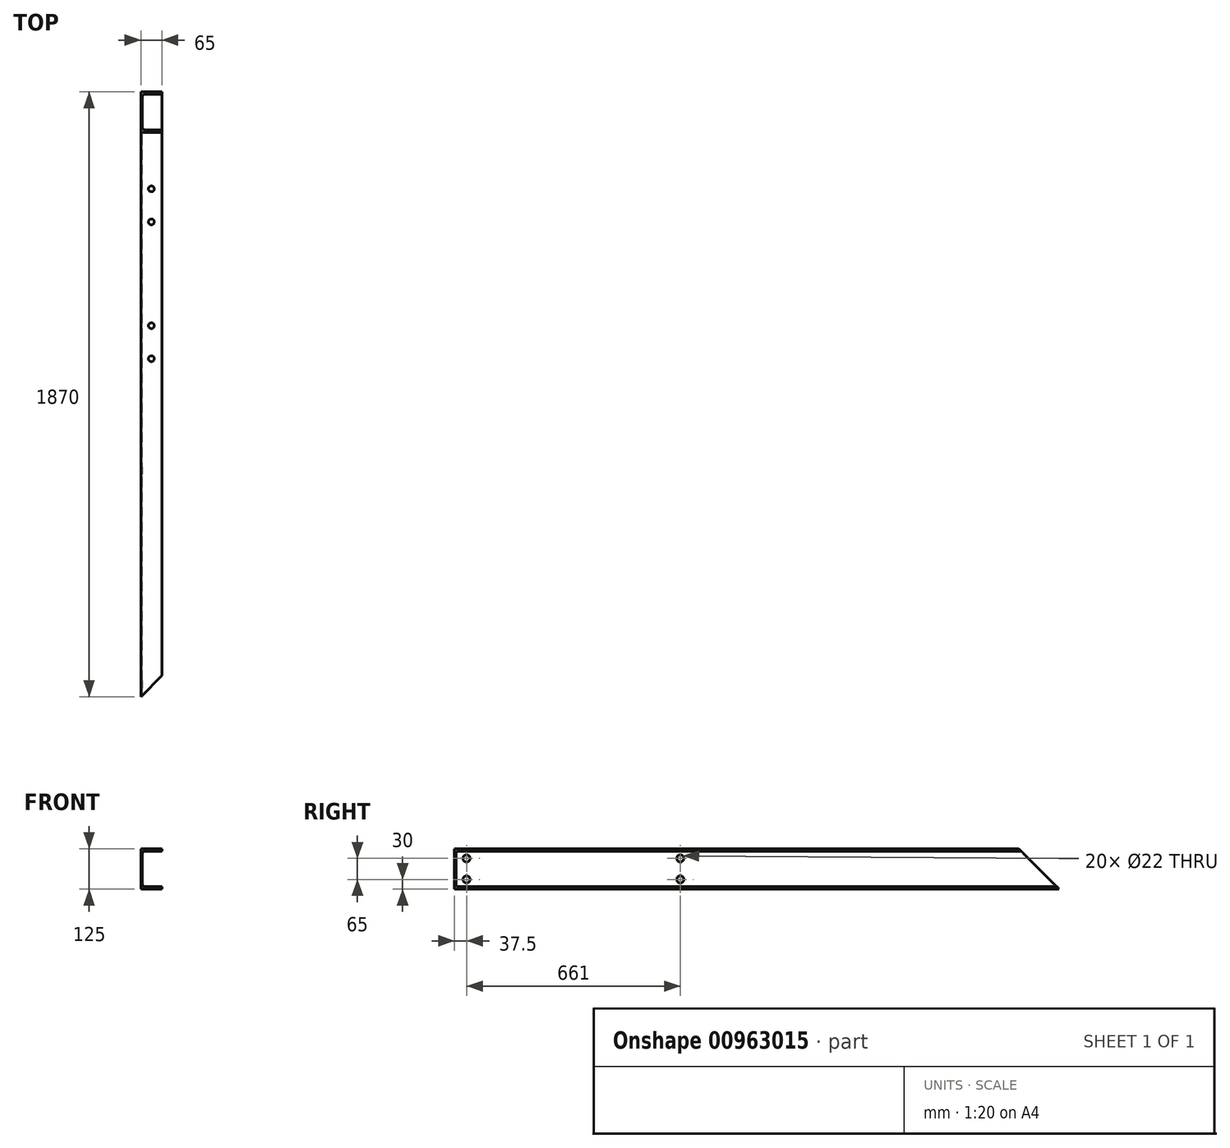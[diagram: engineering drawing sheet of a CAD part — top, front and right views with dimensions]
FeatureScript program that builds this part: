
annotation { "Feature Type Name" : "Feature", "Feature Type Description" : "" }
export const myFeature = defineFeature(function(context is Context, id is Id, definition is map)
    precondition{}
    {
        {
            var Q0;
            Q0=qCreatedBy(makeId("Front.planeOp"),FACE);
            var sketch = newSketch(context, id + "F0", { "sketchPlane" : qUnion([Q0])});
            skLineSegment(sketch, "E0", {"start": v(-25.17, -62.5) * mm, "end": v(-25.17, 62.5) * mm});
            skLineSegment(sketch, "E1", {"start": v(-25.17, 62.5) * mm, "end": v(39.83, 62.5) * mm});
            skLineSegment(sketch, "E2", {"start": v(39.83, 62.5) * mm, "end": v(39.83, 55) * mm});
            skLineSegment(sketch, "E3", {"start": v(39.83, 55) * mm, "end": v(-12.47, 55) * mm});
            skLineSegment(sketch, "E4", {"start": v(-25.17, -62.5) * mm, "end": v(39.83, -62.5) * mm});
            skLineSegment(sketch, "E5", {"start": v(39.83, -62.5) * mm, "end": v(39.83, -55) * mm});
            skLineSegment(sketch, "E6", {"start": v(39.83, -55) * mm, "end": v(-12.47, -55) * mm});
            skLineSegment(sketch, "E7", {"start": v(-20.47, -47) * mm, "end": v(-20.47, 47) * mm});
            skPoint(sketch, "E8.visualSharp", {"position": v(-20.47, 55) * mm});
            skArc(sketch, "E8.filletArc", {"start": v(-12.47, 55) * mm, "mid": v(-18.12, 52.66) * mm, "end": v(-20.47, 47) * mm});
            skPoint(sketch, "E9.visualSharp", {"position": v(-20.47, -55) * mm});
            skArc(sketch, "E9.filletArc", {"start": v(-20.47, -47) * mm, "mid": v(-18.12, -52.66) * mm, "end": v(-12.47, -55) * mm});
            skSolve(sketch);
        }
        {
            var Q0;
            Q0=makeQuery(id+"F0.imprint","IMPRINT",FACE,{"disambiguationData":[TD([[makeQuery(id+"F0.imprint","IMPRINT",EDGE,{"derivedFrom":sQuery(id+"F0.wireOp",EDGE,"E0")}),-1.0]])]});
            extrude(context, id + "F1", {"entities" : qUnion([Q0]), "depth" : 1870 * mm, "offsetDistance" : 25 * mm});
        }
        {
            var Q0;
            Q0=makeQuery(id+"F1.opExtrude","SWEPT_FACE",FACE,{"disambiguationData":[OSD([sQuery(id+"F0.wireOp",EDGE,"E0")])]});
            var sketch = newSketch(context, id + "F2", { "sketchPlane" : qUnion([Q0])});
            skLineSegment(sketch, "E10", {"start": v(0, 62.5) * mm, "end": v(125, 62.5) * mm});
            skLineSegment(sketch, "E11", {"start": v(125, 62.5) * mm, "end": v(0, -62.5) * mm});
            skSolve(sketch);
        }
        {
            var Q0;
            Q0=makeQuery(id+"F2.imprint","IMPRINT",FACE,{"disambiguationData":[TD([[makeQuery(id+"F2.imprint","IMPRINT",EDGE,{"derivedFrom":sQuery(id+"F2.wireOp",EDGE,"E10")}),1.0]])]});
            extrude(context, id + "F3", {"entities" : qUnion([Q0]), "operationType" : NewBodyOperationType.REMOVE, "endBound" : BoundingType.THROUGH_ALL, "oppositeDirection" : true, "depth" : 25 * mm, "offsetDistance" : 25 * mm});
        }
        {
            var Q0;
            Q0=makeQuery(id+"F1.opExtrude","SWEPT_FACE",FACE,{"disambiguationData":[OSD([sQuery(id+"F0.wireOp",EDGE,"E1")])]});
            var sketch = newSketch(context, id + "F4", { "sketchPlane" : qUnion([Q0])});
            skLineSegment(sketch, "E12", {"start": v(39.83, -1870) * mm, "end": v(39.83, -1805) * mm});
            skLineSegment(sketch, "E13", {"start": v(39.83, -1805) * mm, "end": v(-25.17, -1870) * mm});
            skSolve(sketch);
        }
        {
            var Q0;
            Q0=makeQuery(id+"F4.imprint","IMPRINT",FACE,{"disambiguationData":[TD([[makeQuery(id+"F4.imprint","IMPRINT",EDGE,{"derivedFrom":sQuery(id+"F4.wireOp",EDGE,"E12")}),1.0]])]});
            extrude(context, id + "F5", {"entities" : qUnion([Q0]), "operationType" : NewBodyOperationType.REMOVE, "endBound" : BoundingType.THROUGH_ALL, "oppositeDirection" : true, "depth" : 25 * mm, "offsetDistance" : 25 * mm});
        }
        {
            var Q0;
            Q0=makeQuery(id+"F1.opExtrude","SWEPT_FACE",FACE,{"disambiguationData":[OSD([sQuery(id+"F0.wireOp",EDGE,"E1")])]});
            var sketch = newSketch(context, id + "F6", { "sketchPlane" : qUnion([Q0])});
            skLineSegment(sketch, "E14", {"start": v(-25.17, -1870) * mm, "end": v(-25.17, -825) * mm, "construction": true});
            skLineSegment(sketch, "E15", {"start": v(-25.17, -825) * mm, "end": v(7.33, -825) * mm, "construction": true});
            skLineSegment(sketch, "E16", {"start": v(7.33, -825) * mm, "end": v(7.33, -723) * mm, "construction": true});
            skCircle(sketch, "E17", {"center": v(7.33, -723) * mm, "radius": 9 * mm});
            skCircle(sketch, "E18", {"center": v(7.33, -825) * mm, "radius": 9 * mm});
            skSolve(sketch);
        }
        {
            var Q0;
            Q0=qSketchRegion(id+"F6",true);
            extrude(context, id + "F7", {"entities" : qUnion([Q0]), "operationType" : NewBodyOperationType.REMOVE, "endBound" : BoundingType.UP_TO_NEXT, "oppositeDirection" : true, "depth" : 25 * mm, "offsetDistance" : 25 * mm});
        }
        {
            var Q0;
            Q0=makeQuery(id+"F1.opExtrude","SWEPT_FACE",FACE,{"disambiguationData":[OSD([sQuery(id+"F0.wireOp",EDGE,"E1")])]});
            var sketch = newSketch(context, id + "F8", { "sketchPlane" : qUnion([Q0])});
            skCircle(sketch, "E19", {"center": v(7.33, -300) * mm, "radius": 9 * mm});
            skCircle(sketch, "E20", {"center": v(7.33, -402) * mm, "radius": 9 * mm});
            skLineSegment(sketch, "E21", {"start": v(7.33, -300) * mm, "end": v(7.33, -402) * mm, "construction": true});
            skLineSegment(sketch, "E22", {"start": v(7.33, -300) * mm, "end": v(7.33, -125) * mm, "construction": true});
            skSolve(sketch);
        }
        {
            var Q0;
            Q0=qSketchRegion(id+"F8",true);
            extrude(context, id + "F9", {"entities" : qUnion([Q0]), "operationType" : NewBodyOperationType.REMOVE, "endBound" : BoundingType.UP_TO_NEXT, "oppositeDirection" : true, "depth" : 25 * mm, "offsetDistance" : 25 * mm});
        }
        {
            var Q0;
            Q0=makeQuery(id+"F1.opExtrude","SWEPT_FACE",FACE,{"disambiguationData":[OSD([sQuery(id+"F0.wireOp",EDGE,"E0")])]});
            var sketch = newSketch(context, id + "F10", { "sketchPlane" : qUnion([Q0])});
            skLineSegment(sketch, "E23", {"start": v(1870, 62.5) * mm, "end": v(1832.5, 62.5) * mm, "construction": true});
            skLineSegment(sketch, "E24", {"start": v(1832.5, 62.5) * mm, "end": v(1832.5, 32.5) * mm, "construction": true});
            skLineSegment(sketch, "E25", {"start": v(1832.5, 32.5) * mm, "end": v(1832.5, -32.5) * mm, "construction": true});
            skCircle(sketch, "E26", {"center": v(1832.5, 32.5) * mm, "radius": 11 * mm});
            skCircle(sketch, "E27", {"center": v(1832.5, -32.5) * mm, "radius": 11 * mm});
            skLineSegment(sketch, "E28", {"start": v(1832.5, 32.5) * mm, "end": v(1171.5, 32.5) * mm, "construction": true});
            skLineSegment(sketch, "E29", {"start": v(1171.5, 32.5) * mm, "end": v(1171.5, -32.5) * mm, "construction": true});
            skCircle(sketch, "E30", {"center": v(1171.5, 32.5) * mm, "radius": 11 * mm});
            skCircle(sketch, "E31", {"center": v(1171.5, -32.5) * mm, "radius": 11 * mm});
            skSolve(sketch);
        }
        {
            var Q0;
            Q0 = qSketchRegion(id + "F10", true);
            extrude(context, id + "F11", {"entities" : qUnion([Q0]), "operationType" : NewBodyOperationType.REMOVE, "oppositeDirection" : true, "depth" : 25 * mm, "offsetDistance" : 25 * mm});
        }
    });
